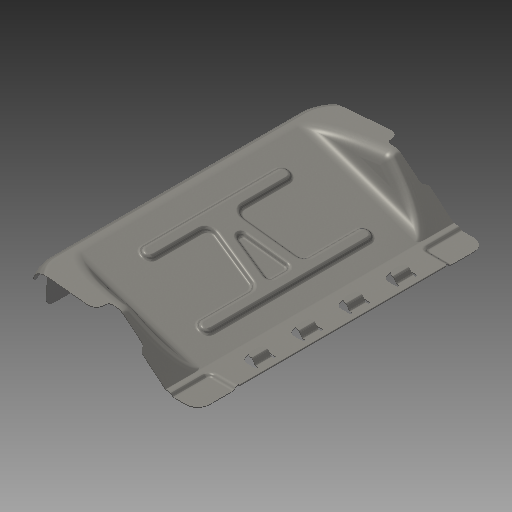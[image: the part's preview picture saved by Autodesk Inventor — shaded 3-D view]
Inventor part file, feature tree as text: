
AUTODESK INVENTOR PART (.ipt)
format: ipt  version: 2019 (Build 230136000, 136)  size: 1,317,376 bytes
history: native  units: mm
features: extrude x16, fillet x16, sketch x16, chamfer x3, mirror x3, shell x1, plane x1, pattern_linear x1, other x1, projected_geometry x1
ambient origin geometry x8: Origin, YZ Plane, XZ Plane, XY Plane, X Axis, Y Axis, Z Axis, Center Point
bodies: Solid1 (feature_tree)
feature tree (59):
  extrude  "Extrusion1"  Depth=19.268807mm
  extrude  "Extrusion2"  Depth=83.897104mm
  chamfer  "Chamfer1"  Distance=435.0mm
  mirror  "Mirror1"
  extrude  "Extrusion3"  Depth=2.5mm
  chamfer  "Chamfer2"  Distance=387.019492mm
  chamfer  "Chamfer3"  Distance=34.0mm Angle=45.0deg
  fillet  "Fillet3"  Radius=53.412945mm
  fillet  "Fillet8"  Radius=83.897104mm
  fillet  "Fillet9"  Radius=71.789805mm
  fillet  "Fillet10"  Radius=130.0mm
  fillet  "Fillet13"  Radius=328.0mm
  fillet  "Fillet14"  Radius=20.0mm
  shell  "Shell1"  Thickness=20.0mm
  extrude  "Extrusion4"  Depth=20.0mm
  extrude  "Extrusion5"  Depth=1.0mm
  fillet  "Fillet11"  Radius=184.0mm
  fillet  "Fillet12"  Radius=103.0mm
  mirror  "Mirror2"
  extrude  "Extrusion7"  Depth=4.75mm
  extrude  "Extrusion8"  Depth=44.0mm
  extrude  "Extrusion9"  Depth=6.5mm
  mirror  "Mirror4"
  fillet  "Fillet15"  Radius=130.0mm
  fillet  "Fillet16"  Radius=220.0mm
  extrude  "Extrusion11"  Depth=10.0mm
  fillet  "Fillet17"  Radius=300.0mm
  extrude  "Extrusion12"  Depth=46.0mm
  extrude  "Extrusion13"  Depth=10.0mm
  extrude  "Extrusion17"  Depth=10.0mm
  fillet  "Fillet18"  Radius=10.0mm
  extrude  "Extrusion14"  Depth=0.25mm
  fillet  "Fillet19"  Radius=123.0mm
  plane  "Work Plane1"
  extrude  "Extrusion15"  Depth=10.0mm
  extrude  "Extrusion16"  Depth=0.25mm
  pattern_linear  "Rectangular Pattern1"  Spacing1=2.5mm  [1 undecoded]
  fillet  "Fillet20"  Radius=5.0mm
  fillet  "Fillet21"  Radius=1.0mm
  extrude  "Extrusion18"  Depth=0.25mm
  fillet  "Fillet22"  Radius=46.0mm
  other  "Work Point1"
  sketch  "Sketch2"  dims[d0=89.79065mm d1=19.268807mm]
  sketch  "Sketch3"  dims[d2=24.509865mm d3=83.897104mm]
  sketch  "Sketch4"  dims[d4=53.412945mm d6=435.0mm d7=0.0mm]
  sketch  "Sketch5"  dims[d8=155.0mm d10=2.5mm d12=387.019492mm d13=0.0mm]
  sketch  "Sketch6"  dims[d14=100.0mm d16=34.0mm d17=30.0mm d18=45.0deg d19=53.412945mm d20=83.897104mm d21=71.789805mm d22=130.0mm d23=328.0mm d24=0.0mm]
  sketch  "Sketch8"  dims[d25=29.543mm d26=15.0mm d27=45.0deg]
  sketch  "Sketch9"  dims[d28=29.543mm d29=15.0mm d30=45.0deg d33=20.0mm d38=20.0mm]
  sketch  "Sketch10"  dims[d40=20.0mm d41=20.0mm]
  sketch  "Sketch12"  dims[d42=15.0mm d43=1.0mm d44=184.0mm d45=103.0mm]
  sketch  "Sketch13"  dims[d46=0.916298mm d47=4.75mm]
  sketch  "Sketch14"  dims[d48=177.0mm d49=44.0mm]
  sketch  "Sketch15"  dims[d50=20.245819mm d51=6.5mm d52=130.0mm d53=220.0mm]
  sketch  "Sketch17"  dims[d54=10.0mm d55=4.0mm d56=300.0mm d57=0.0mm]
  sketch  "Sketch18"  dims[d58=50.0mm d59=46.0mm]
  sketch  "Sketch19"  dims[d60=37.0mm d61=10.0mm]
  sketch  "Sketch20"  dims[d62=25.0mm d63=0.0mm d64=10.0mm d65=10.0mm d66=4.0mm d70=123.0mm d71=10.0mm d72=0.785398mm d73=2.5mm d74=5.0mm d75=1.0mm d76=46.0mm d77=46.0mm d78=30.0mm d79=275.0mm d80=0.0mm d81=1.0mm d82=1.0mm d83=3.394105mm d84=0.0mm d85=1.0mm d86=0.0mm d87=5.0mm d88=6.0mm d89=4.75mm d90=5.75mm d93=2.5mm d94=0.0mm d95=15.0mm d96=185.0mm d104=70.0mm d105=108.0mm d106=7.5mm d107=15.0mm d108=15.0mm d109=200.0mm d110=10.0mm d111=27.106309mm d112=27.106309mm d113=38.260156mm d114=38.260156mm d115=55.0mm d116=23.0mm d117=92.5mm d118=100.0mm d119=1.0mm d120=0.0mm d121=1.0mm d122=4.0mm d123=0.0mm d124=5.0mm d125=4.0mm d126=26.0mm d128=30.0mm d129=21.0mm d130=13.0mm d131=6.0mm d132=20.0mm d134=60.0mm d135=10.0mm d137=10.0mm d139=30.0mm d141=60.0mm d142=10.0mm d144=10.0mm d146=1.0mm d147=0.0mm d148=15.0mm d150=15.0mm d151=5.0mm d152=1.0mm d153=8.0mm d154=1.0mm d155=1.0mm d156=4.5mm d157=10.12291mm d158=8.726646mm d159=8.5mm d160=7.25mm d161=3.0mm d162=4.0mm d163=20.0mm d164=0.0mm d165=40.0mm d166=1.0mm d167=0.0mm d168=4.0mm d169=2.0mm d170=40.0mm d172=60.0mm d173=3.0mm d174=0.0mm d177=263.0mm d178=0.0mm d179=0.25mm d180=0.1mm d181=1.5mm d182=0.25mm]
  projected_geometry  "Project Cut Edges1"
note: 1 required parameter value undecoded (feature->parameter linkage not recoverable at this tier; creation-order binding heuristic only, values carry confidence <= 0.55)
